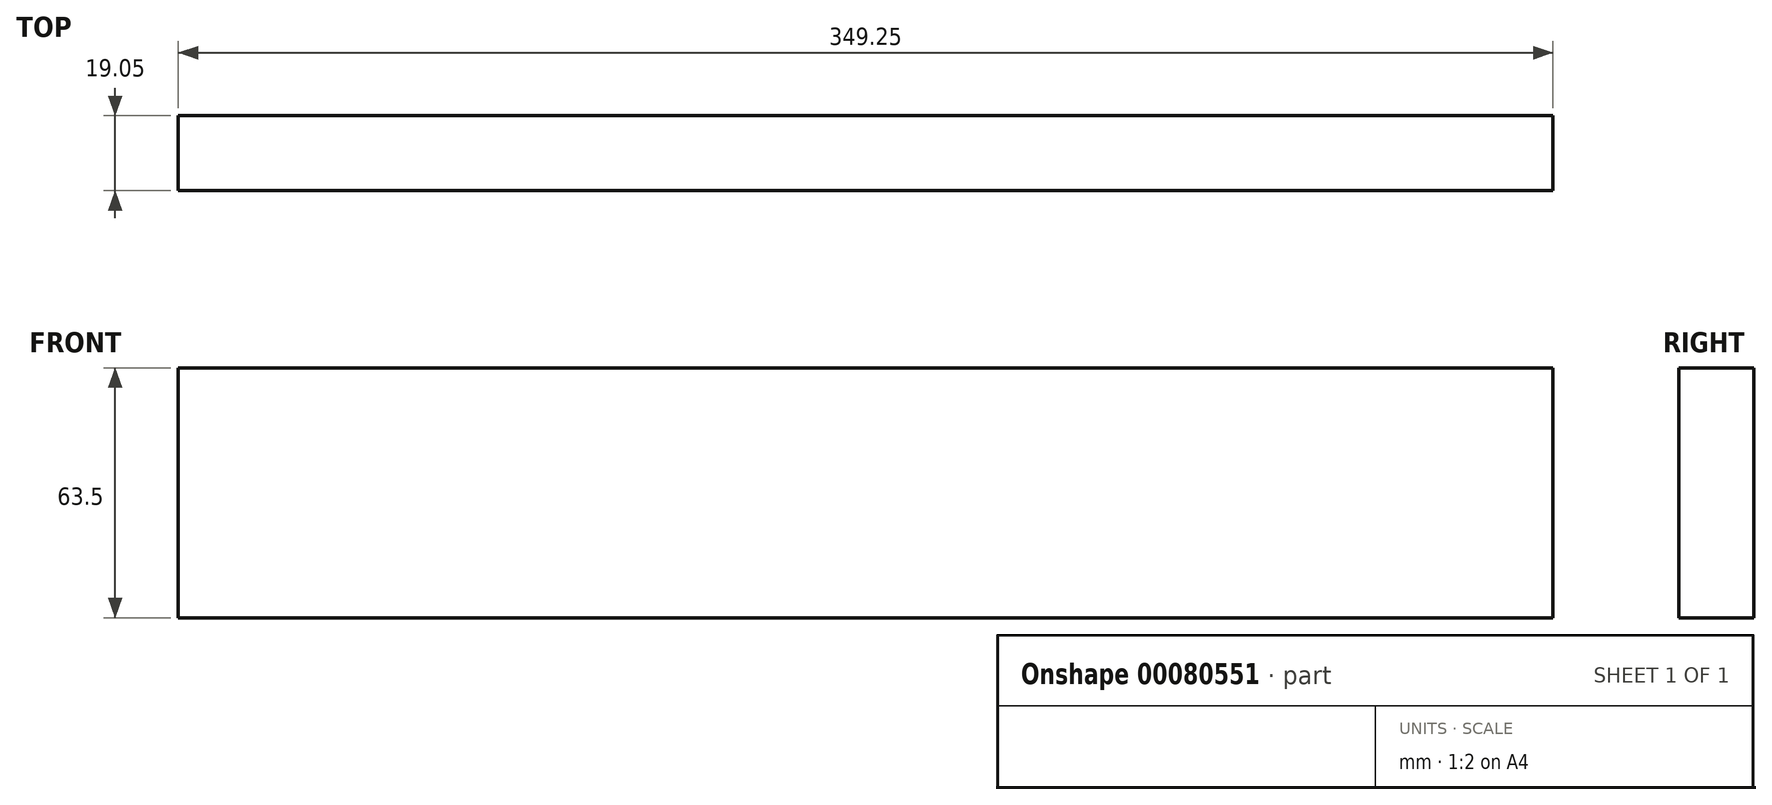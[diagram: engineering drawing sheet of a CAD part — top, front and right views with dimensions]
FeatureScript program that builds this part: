
annotation { "Feature Type Name" : "Feature", "Feature Type Description" : "" }
export const myFeature = defineFeature(function(context is Context, id is Id, definition is map)
    precondition{}
    {
        {
            var Q0;
            Q0=qCreatedBy(makeId("Front.planeOp"),FACE);
            var sketch = newSketch(context, id + "F0", { "sketchPlane" : qUnion([Q0])});
            skLineSegment(sketch, "E0.bottom", {"start": v(0, 0) * mm, "end": v(-349.25, 0) * mm});
            skLineSegment(sketch, "E0.top", {"start": v(0, 63.5) * mm, "end": v(-349.25, 63.5) * mm});
            skLineSegment(sketch, "E0.left", {"start": v(0, 0) * mm, "end": v(0, 63.5) * mm});
            skLineSegment(sketch, "E0.right", {"start": v(-349.25, 0) * mm, "end": v(-349.25, 63.5) * mm});
            skSolve(sketch);
        }
        {
            var Q0;
            Q0=makeQuery(id+"F0.imprint","IMPRINT",FACE,{"disambiguationData":[TD([[makeQuery(id+"F0.imprint","IMPRINT",EDGE,{"derivedFrom":sQuery(id+"F0.wireOp",EDGE,"E0.bottom")}),-1.0]])]});
            extrude(context, id + "F1", {"entities" : qUnion([Q0]), "depth" : 19.05 * mm});
        }
    });
